# Revit family: TMS-Luna-Zest-Pendant
name_source: partatom
category: Lighting Fixtures
units: mm (PartAtom-declared; Revit-internal decimal feet)

## family parameters
Cut with Voids When Loaded = No
Host = Face
Light Source = Yes
Part Type = Normal
Room Calculation Point = No
Round Connector Dimension = Use Diameter
Shared = No

## types (14) — shared parameters
Acoustic Material = TMS Fabric Linen Blue
Apparent Load = 0 VA
Assembly Code = D5020200
Cable Material = Steel
Canopy Material = TMS Gloss Black
Color Filter = 16777215
Default Elevation = 4' - 0"
Dimming Lamp Color Temperature Shift = <None>
Fixture Material = TMS Gloss Black
Lens Material = TMS Lens
Manufacturer = TMS Lighting Inc.
Model = LUNA ZEST
Number of Poles = 1
Power Factor = 1
Support Material = TMS Gloss Black
Tilt Angle = -90.00°
URL = https://tmslighting.com
Voltage = 0 V

## per-type parameters (varying)
| type | Length | Photometric Web File | Support Distance | Support Length | Support Width | Top Fixture Material | Width |
| 5L3W | 5' - 0" | 941LURSCL 5L3WD 35K F05.ies | 0' - 4" | 4' - 5" | 2' - 5" | TMS Gloss Black | 3' - 0" |
| 6L3W | 6' - 0" | 941LURSCL 6L3WD 35K F05.ies | 0' - 4" | 5' - 5" | 2' - 5" | TMS Gloss Black | 3' - 0" |
| 7L3W | 7' - 0" | 941LURSCL 7L3WD 35K F05.ies | 0' - 3 3/4" | 6' - 5" | 2' - 5" | TMS Gloss Black | 3' - 0" |
| 7L4W | 7' - 0" | 941LURSCL 7L4WD 35K F05.ies | 0' - 3 3/4" | 6' - 5" | 3' - 5" | TMS Gloss Black | 4' - 0" |
| 8L3W | 8' - 0" | 941LURSCL 8L3WD 35K F05.ies | 0' - 3 3/4" | 7' - 5" | 2' - 5" | TMS Gloss Black | 3' - 0" |
| 8L4W | 8' - 0" | 941LURSCL 8L4WD 35K F05.ies | 0' - 3 3/4" | 7' - 5" | 3' - 5" | TMS Gloss Black | 4' - 0" |
| 5L3W Direct/Indirect | 5' - 0" | 941LURSP 5L3WID TA 35K F05.ies | 0' - 4" | 4' - 5" | 2' - 5" | TMS Lens | 3' - 0" |
| 6L3W Direct/Indirect | 6' - 0" | 941LURSP 6L3WID TA 35K F05.ies | 0' - 4" | 5' - 5" | 2' - 5" | TMS Lens | 3' - 0" |
| 7L3W Direct/Indirect | 7' - 0" | 941LURSP 7L3WID TA 35K F05.ies | 0' - 3 3/4" | 6' - 5" | 2' - 5" | TMS Lens | 3' - 0" |
| 7L4W Direct/Indirect | 7' - 0" | 941LURSP 7L4WID TA 35K F05.ies | 0' - 3 3/4" | 6' - 5" | 3' - 5" | TMS Lens | 4' - 0" |
| 8L3W Direct/Indirect | 8' - 0" | 941LURSP 8L3WID TA 35K F05.ies | 0' - 3 3/4" | 7' - 5" | 2' - 5" | TMS Lens | 3' - 0" |
| 8L4W Direct/Indirect | 8' - 0" | 941LURSP 8L4WID TA 35K F05.ies | 0' - 3 3/4" | 7' - 5" | 3' - 5" | TMS Lens | 4' - 0" |
| 8L5W | 8' - 0" | 941LURSP 8L5WD 35K F05.ies | 0' - 3 3/4" | 7' - 5" | 4' - 5" | TMS Gloss Black | 5' - 0" |
| 8L5W Direct/Indirect | 8' - 0" | 941LURSP 8L5WID 35K F05.ies | 0' - 3 3/4" | 7' - 5" | 4' - 5" | TMS Lens | 5' - 0" |

## geometry (parser evidence)
native form markers: Sweep x9
no freeform markers — native parametric forms only
